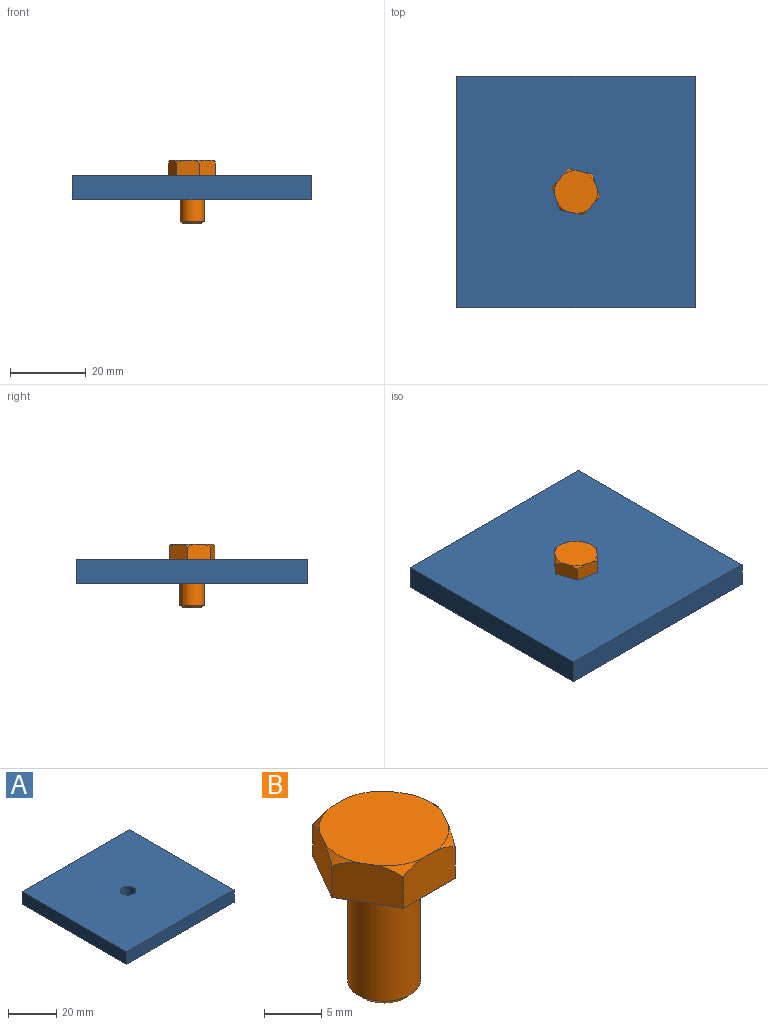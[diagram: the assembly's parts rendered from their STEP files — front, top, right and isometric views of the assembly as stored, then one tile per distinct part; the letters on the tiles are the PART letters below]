
ASSEMBLY  parts=2 mates=1
PART A: 7 faces, bbox 63x61.1x6.4 mm
  f0: plane 61.14x6.35mm, normal (1,0,0), area 388.2mm2, adj f1,f4,f5,f6
  f1: plane 62.96x6.35mm, normal (0,1,0), area 399.8mm2, adj f0,f2,f5,f6
  f2: plane 61.14x6.35mm, normal (-1,0,0), area 388.2mm2, adj f1,f4,f5,f6
  f3: cylinder r=3.17mm len=6.35mm, axis (0,0,1), area 126.7mm2, adj f5,f6
  f4: plane 62.96x6.35mm, normal (0,-1,0), area 399.8mm2, adj f0,f2,f5,f6
  f5: plane 62.96x61.14mm, normal (0,0,-1), area 3817.4mm2, adj f0,f1,f2,f3,f4
  f6: plane 62.96x61.14mm, normal (0,0,1), area 3817.4mm2, adj f0,f1,f2,f3,f4
PART B: 18 faces, bbox 12.9x12.6x16.8 mm
  f0: plane 5.08x5.08mm, normal (0,0,-1), area 20.3mm2, adj f17
  f1: cylinder r=3.17mm len=11.75mm, axis (0,0,-1), area 234.4mm2, adj f16,f17
  f2: plane 12.85x11.13mm, normal (0,0,-1), area 68.9mm2, adj f3,f4,f5,f6,f7,f8,f16
  f3: plane 5.57x4.14mm, normal (0.87,0.5,0), area 25.2mm2, adj f2,f4,f6,f9,f13,f15
  f4: plane 6.43x4.14mm, normal (0,1,0), area 25.2mm2, adj f2,f3,f5,f9,f14,f15
  f5: plane 5.57x4.14mm, normal (-0.87,0.5,0), area 25.2mm2, adj f2,f4,f7,f9,f12,f14
  f6: plane 5.57x4.14mm, normal (0.87,-0.5,0), area 25.2mm2, adj f2,f3,f8,f9,f11,f13
  f7: plane 5.57x4.14mm, normal (-0.87,-0.5,0), area 25.2mm2, adj f2,f5,f8,f9,f10,f12
  f8: plane 6.43x4.14mm, normal (0,-1,0), area 25.2mm2, adj f2,f6,f7,f9,f10,f11
  f9: plane 11.32x11.13mm, normal (0,0,1), area 99.9mm2, adj f3,f4,f5,f6,f7,f8,f10,f11
  f10: cone r=5.66mm half-angle=45deg, axis (0,0,-1), area 1.7mm2, adj f7,f8,f9
  f11: cone r=5.66mm half-angle=45deg, axis (0,0,-1), area 1.7mm2, adj f6,f8,f9
  f12: cone r=5.66mm half-angle=45deg, axis (0,0,-1), area 1.7mm2, adj f5,f7,f9
  f13: cone r=5.66mm half-angle=45deg, axis (0,0,-1), area 1.7mm2, adj f3,f6,f9
  f14: cone r=5.66mm half-angle=45deg, axis (0,0,-1), area 1.7mm2, adj f4,f5,f9
  f15: cone r=5.66mm half-angle=45deg, axis (0,0,-1), area 1.7mm2, adj f3,f4,f9
  f16: torus R=3.49mm, axis (0,0,1), area 10.3mm2, adj f1,f2
  f17: cone r=2.54mm half-angle=45deg, axis (0,0,1), area 16.1mm2, adj f0,f1
PLACE A at identity fixed
PLACE B rot(axis=(0,0,1),49.2deg) t=(0,0,-25.4)mm
MATE cylindrical B.f1 <-> A.f3  axis (0,0,1) through (0,0,0)mm
